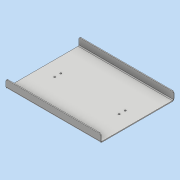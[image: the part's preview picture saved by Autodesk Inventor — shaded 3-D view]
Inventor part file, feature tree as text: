
AUTODESK INVENTOR PART (.ipt)
format: ipt  version: 2018 (Build 220112000, 112)  size: 161,792 bytes
history: native  units: mm
features: other x12, reference x4, sketch x3, hole x1
ambient origin geometry x8: Origin, YZ Plane, XZ Plane, XY Plane, X Axis, Y Axis, Z Axis, Center Point
bodies: Volumenkörper1 (feature_tree)
feature tree (20):
  other  "Fläche1"
  other  "Lasche1"
  hole  "Bohrung1"  [1 undecoded]
  other  "Eckenrundung1"
  sketch  "Skizze1"  dims[d0=230.0mm d1=180.0mm]
  other  "Grobblech1"
  sketch  "Skizze2"  dims[d2=2.0mm]
  other  "Grobblech2"
  other  "Biegung1"
  other  "Ecke1"
  sketch  "Skizze3"  dims[d3=2.0mm d4=1.0mm d5=4.0mm d6=2.0mm d7=20.0mm d8=90.0deg d9=2.0mm d10=8.0mm d11=2.0mm d12=2.0mm d13=3.0mm d14=4.0mm d15=6.0mm d16=4.0mm d17=2.0mm d18=90.0deg d19=2.0mm d20=20.594885mm]
  reference  "Referenz1"
  reference  "Referenz2"
  reference  "Referenz3"
  reference  "Referenz4"
  other  "Definition1"
  other  "<userpath>\Documents\Waage\CAD\Main.iam"
  other  "Main.iam"
  other  "LoadCell:2"
  other  "LoadCell:3"
note: 1 required parameter value undecoded (feature->parameter linkage not recoverable at this tier; creation-order binding heuristic only, values carry confidence <= 0.55)
